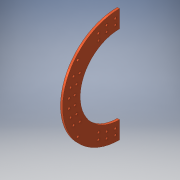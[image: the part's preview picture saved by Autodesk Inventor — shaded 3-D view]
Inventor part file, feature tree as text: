
AUTODESK INVENTOR PART (.ipt)
format: ipt  version: 2016 (Build 200138000, 138)  size: 148,992 bytes
history: native  units: in
note: dims shown in document units (in); Inventor stores cm internally (conversion verified against a paired STEP export)
features: sketch x2, extrude x2, hole x1, plane x1, mirror x1, reference x1
ambient origin geometry x8: Origin, YZ Plane, XZ Plane, XY Plane, X Axis, Y Axis, Z Axis, Center Point
bodies: Solid1 (feature_tree)
feature tree (8):
  sketch  "Sketch1"  dims[d1=9.0in d2=2.0in]
  extrude  "Extrusion1"  Depth=2.0in
  hole  "Hole1"  [1 undecoded]
  extrude  "Extrusion2"  Depth=0.25in
  plane  "Work Plane1"
  mirror  "Mirror1"
  sketch  "Sketch2"  dims[d3=10.3in d4=13.0in d5=11.6in d6=1.0in d7=1.0in d8=0.5in d9=0.5in d10=1.0in d11=1.0in d12=45.0deg d13=45.0deg d14=0.25in d15=0.0in d16=0.26in d17=0.75in d18=0.375in d19=0.25in d20=0.5635in d21=1.0in d22=0.8108in d23=1.0in d24=0.0in]
  reference  "Reference1"
note: 1 required parameter value undecoded (feature->parameter linkage not recoverable at this tier; creation-order binding heuristic only, values carry confidence <= 0.55)
